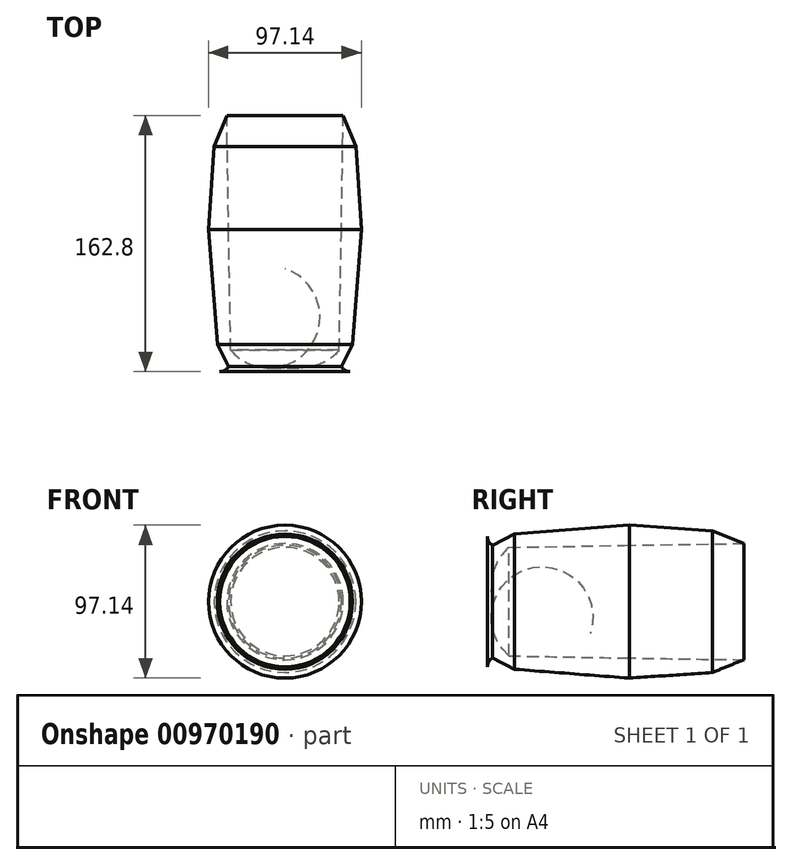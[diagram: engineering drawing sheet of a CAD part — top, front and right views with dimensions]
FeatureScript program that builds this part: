
annotation { "Feature Type Name" : "Feature", "Feature Type Description" : "" }
export const myFeature = defineFeature(function(context is Context, id is Id, definition is map)
    precondition{}
    {
        {
            var Q0;
            Q0=qCreatedBy(makeId("Top.planeOp"),FACE);
            var sketch = newSketch(context, id + "F0", { "sketchPlane" : qUnion([Q0])});
            skLineSegment(sketch, "E0", {"start": v(-36.93, 75.9) * mm, "end": v(-44.96, 56.05) * mm});
            skLineSegment(sketch, "E1", {"start": v(-44.96, 56.05) * mm, "end": v(-48.57, 3.33) * mm});
            skLineSegment(sketch, "E2", {"start": v(-48.57, 3.33) * mm, "end": v(-42.94, -69.63) * mm});
            skLineSegment(sketch, "E3", {"start": v(-42.94, -69.63) * mm, "end": v(-34.22, -86.89) * mm});
            skPoint(sketch, "E4.orphan", {"position": v(0, -154.54) * mm});
            skLineSegment(sketch, "E5", {"start": v(0, -154.54) * mm, "end": v(0, 75.6) * mm});
            skLineSegment(sketch, "E6", {"start": v(-34.22, -86.89) * mm, "end": v(-35.78, 0) * mm});
            skLineSegment(sketch, "E7", {"start": v(-35.78, 0) * mm, "end": v(-36.93, 75.9) * mm});
            skLineSegment(sketch, "E8", {"start": v(-34.22, -86.89) * mm, "end": v(0, -86.89) * mm});
            skLineSegment(sketch, "E9", {"start": v(0, -86.89) * mm, "end": v(0, -82.82) * mm});
            skArc(sketch, "E10", {"start": v(-34.46, -73.25) * mm, "mid": v(-18.68, -83.25) * mm, "end": v(0, -82.82) * mm});
            skLineSegment(sketch, "E11", {"start": v(-34.22, -86.89) * mm, "end": v(-41.47, -86.89) * mm});
            skArc(sketch, "E12", {"start": v(-41.47, -86.89) * mm, "mid": v(-38.23, -86.04) * mm, "end": v(-35.81, -83.73) * mm});
            skSolve(sketch);
        }
        {
            var Q0;
            Q0=makeQuery(id+"F0.imprint","IMPRINT",FACE,{"disambiguationData":[TD([[makeQuery(id+"F0.imprint","IMPRINT",EDGE,{"derivedFrom":sQuery(id+"F0.wireOp",EDGE,"E0")}),1.0]])]});
            var Q1;
            {var subQ0=sQuery(id+"F0.wireOp",EDGE,"E8");Q1=makeQuery(id+"F0.imprint","IMPRINT",FACE,{"disambiguationData":[TD([[makeQuery(id+"F0.imprint","IMPRINT",EDGE,{"derivedFrom":subQ0}),1.0]])]});}
            var Q2;
            {var subQ0=sQuery(id+"F0.wireOp",EDGE,"E11");Q2=makeQuery(id+"F0.imprint","IMPRINT",FACE,{"disambiguationData":[TD([[makeQuery(id+"F0.imprint","IMPRINT",EDGE,{"derivedFrom":subQ0}),-1.0]])]});}
            var Q3;
            Q3=sQuery(id+"F0.wireOp",EDGE,"E5");
            revolve(context, id + "F1", {"surfaceOperationType" : NewSurfaceOperationType.NEW, "entities" : qUnion([Q0, Q1, Q2]), "axis" : qUnion([Q3]), "revolveType" : RevolveType.FULL});
        }
    });
